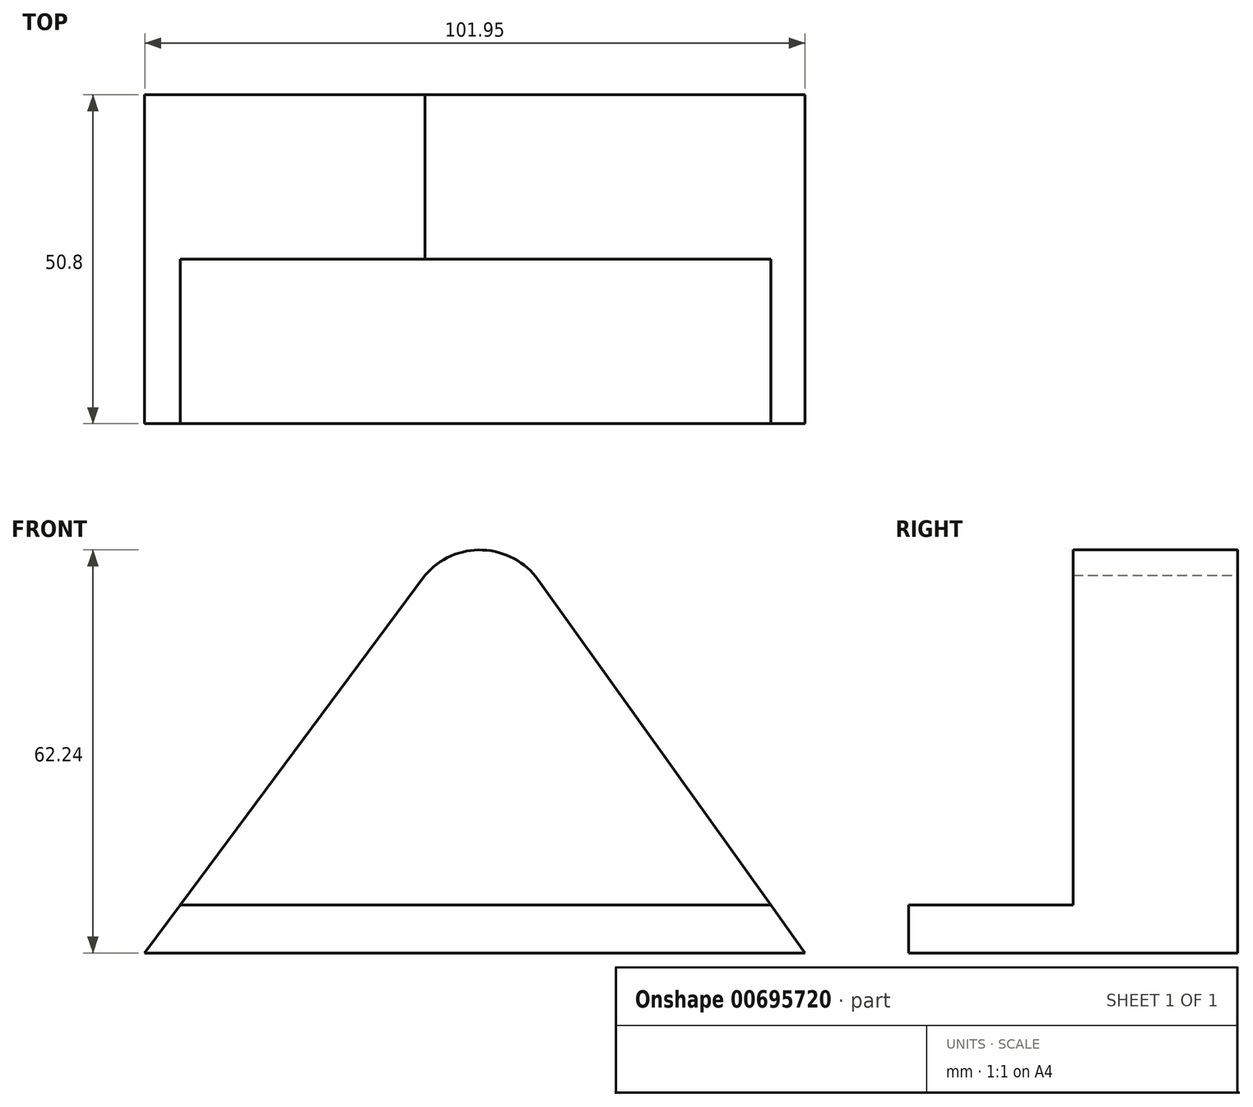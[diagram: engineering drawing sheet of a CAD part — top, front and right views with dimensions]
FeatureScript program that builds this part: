
annotation { "Feature Type Name" : "Feature", "Feature Type Description" : "" }
export const myFeature = defineFeature(function(context is Context, id is Id, definition is map)
    precondition{}
    {
        {
            var Q0;
            Q0=qCreatedBy(makeId("Front.planeOp"),FACE);
            var sketch = newSketch(context, id + "F0", { "sketchPlane" : qUnion([Q0])});
            skLineSegment(sketch, "E0", {"start": v(-70.24, 13.44) * mm, "end": v(-26.95, 71.75) * mm});
            skLineSegment(sketch, "E1", {"start": v(-9.49, 71.06) * mm, "end": v(31.71, 13.44) * mm});
            skArc(sketch, "E2", {"start": v(-9.49, 71.06) * mm, "mid": v(-18.05, 75.67) * mm, "end": v(-26.95, 71.75) * mm});
            skLineSegment(sketch, "E3", {"start": v(-70.24, 13.44) * mm, "end": v(31.71, 13.44) * mm});
            skSolve(sketch);
        }
        {
            var Q0;
            Q0 = qSketchRegion(id + "F0", true);
            extrude(context, id + "F1", {"entities" : qUnion([Q0]), "depth" : 25.4 * mm, "offsetDistance" : 25.4 * mm});
        }
        {
            var Q0;
            Q0=makeQuery(id+"F1.opExtrude","CAP_FACE",FACE,{"disambiguationData":[OSD([sQuery(id+"F0.wireOp",EDGE,"E0"),sQuery(id+"F0.wireOp",EDGE,"E1"),sQuery(id+"F0.wireOp",EDGE,"E2"),sQuery(id+"F0.wireOp",EDGE,"E3")])],"isStart":false});
            var sketch = newSketch(context, id + "F2", { "sketchPlane" : qUnion([Q0])});
            skLineSegment(sketch, "E4.bottom", {"start": v(-70.24, 13.44) * mm, "end": v(31.71, 13.44) * mm});
            skLineSegment(sketch, "E4.top", {"start": v(-64.74, 20.85) * mm, "end": v(26.42, 20.85) * mm});
            skLineSegment(sketch, "E5", {"start": v(31.71, 13.44) * mm, "end": v(26.42, 20.85) * mm});
            skLineSegment(sketch, "E6", {"start": v(-70.24, 13.44) * mm, "end": v(-64.74, 20.85) * mm});
            skPoint(sketch, "E4.right.end.orphan", {"position": v(31.71, 20.85) * mm});
            skSolve(sketch);
        }
        {
            var Q0;
            Q0 = qSketchRegion(id + "F2", true);
            extrude(context, id + "F3", {"entities" : qUnion([Q0]), "operationType" : NewBodyOperationType.ADD, "depth" : 25.4 * mm, "offsetDistance" : 25.4 * mm});
        }
    });
